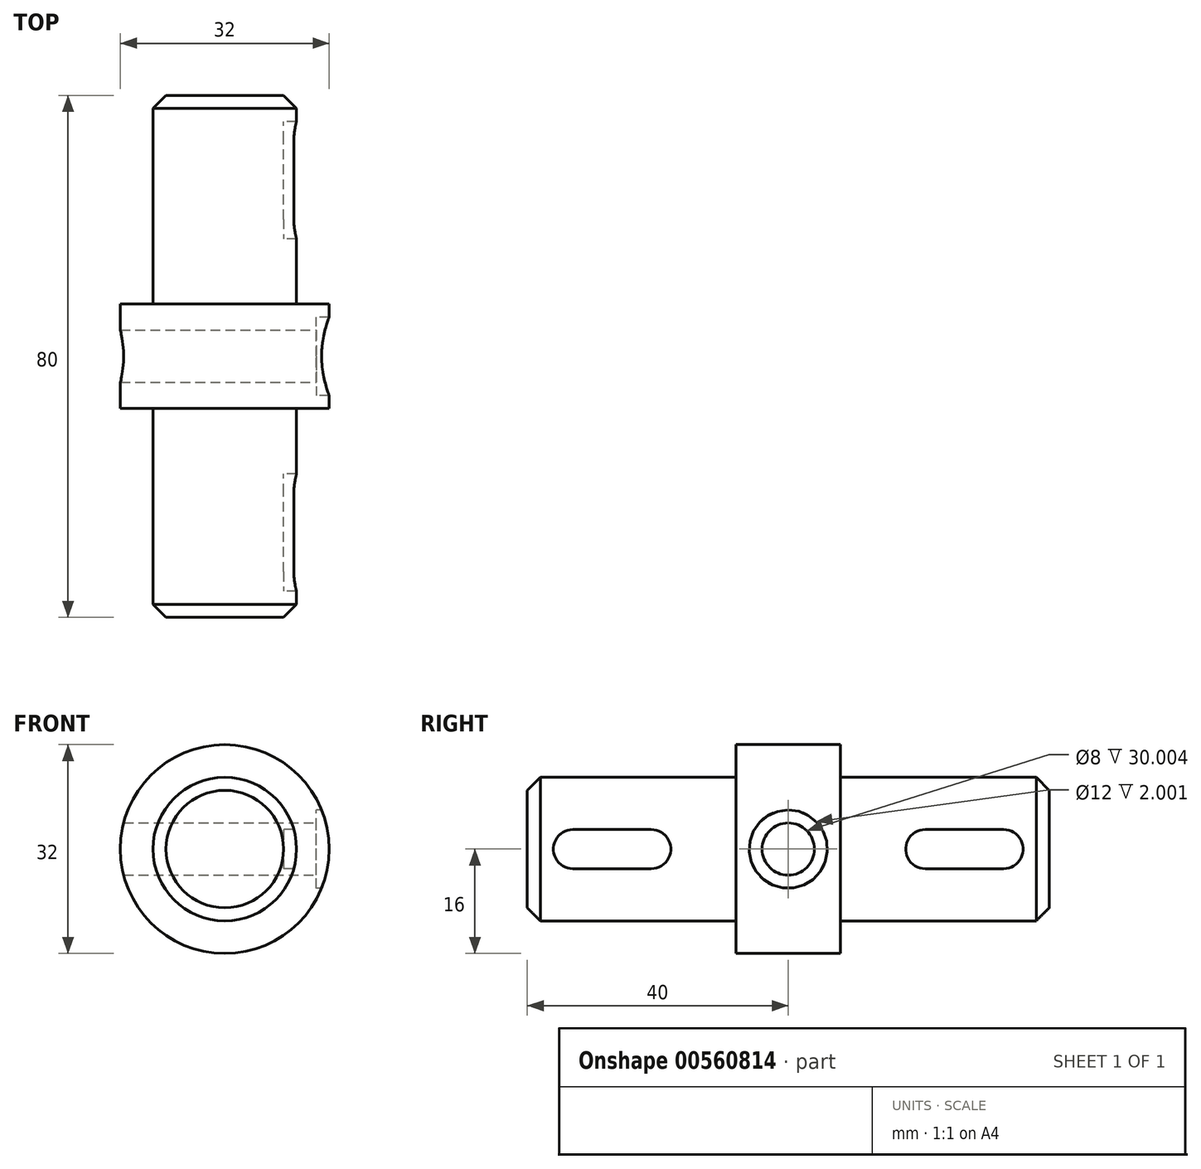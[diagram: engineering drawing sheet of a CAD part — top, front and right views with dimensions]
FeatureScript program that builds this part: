
annotation { "Feature Type Name" : "Feature", "Feature Type Description" : "" }
export const myFeature = defineFeature(function(context is Context, id is Id, definition is map)
    precondition{}
    {
        {
            var Q0;
            Q0=qCreatedBy(makeId("Front.planeOp"),FACE);
            var sketch = newSketch(context, id + "F0", { "sketchPlane" : qUnion([Q0])});
            skCircle(sketch, "E0", {"center": v(0, 0) * mm, "radius": 11 * mm});
            skSolve(sketch);
        }
        {
            var Q0;
            Q0 = qSketchRegion(id + "F0", true);
            extrude(context, id + "F1", {"entities" : qUnion([Q0]), "endBound" : BoundingType.SYMMETRIC, "depth" : 80 * mm, "offsetDistance" : 25 * mm});
        }
        {
            var Q0;
            Q0=qCreatedBy(makeId("Front.planeOp"),FACE);
            var sketch = newSketch(context, id + "F2", { "sketchPlane" : qUnion([Q0])});
            skCircle(sketch, "E1", {"center": v(0, 0) * mm, "radius": 16 * mm});
            skSolve(sketch);
        }
        {
            var Q0;
            Q0 = qSketchRegion(id + "F2", true);
            extrude(context, id + "F3", {"entities" : qUnion([Q0]), "operationType" : NewBodyOperationType.ADD, "endBound" : BoundingType.SYMMETRIC, "depth" : 16 * mm, "offsetDistance" : 25 * mm});
        }
        {
            var Q0;
            Q0=qCreatedBy(makeId("Right.planeOp"),FACE);
            var sketch = newSketch(context, id + "F4", { "sketchPlane" : qUnion([Q0])});
            skCircle(sketch, "E2", {"center": v(0, 0) * mm, "radius": 4 * mm});
            skSolve(sketch);
        }
        {
            var Q0;
            Q0 = qSketchRegion(id + "F4", true);
            extrude(context, id + "F5", {"entities" : qUnion([Q0]), "operationType" : NewBodyOperationType.REMOVE, "endBound" : BoundingType.SYMMETRIC, "oppositeDirection" : true, "depth" : 50 * mm, "offsetDistance" : 25 * mm});
        }
        {
            var Q0;
            Q0=qCreatedBy(makeId("Right.planeOp"),FACE);
            var sketch = newSketch(context, id + "F6", { "sketchPlane" : qUnion([Q0])});
            skCircle(sketch, "E3", {"center": v(0, 0) * mm, "radius": 6 * mm});
            skSolve(sketch);
        }
        {
            var Q0;
            Q0 = qSketchRegion(id + "F6", true);
            extrude(context, id + "F7", {"entities" : qUnion([Q0]), "operationType" : NewBodyOperationType.REMOVE, "depth" : 25 * mm, "offsetDistance" : 25 * mm});
        }
        {
            var Q0;
            Q0=qCreatedBy(makeId("Right.planeOp"),FACE);
            var sketch = newSketch(context, id + "F8", { "sketchPlane" : qUnion([Q0])});
            skCircle(sketch, "E4", {"center": v(0, 0) * mm, "radius": 6 * mm});
            skCircle(sketch, "E5", {"center": v(0, 0) * mm, "radius": 4 * mm});
            skSolve(sketch);
        }
        {
            var Q0;
            Q0 = qSketchRegion(id + "F8", true);
            extrude(context, id + "F9", {"entities" : qUnion([Q0]), "operationType" : NewBodyOperationType.ADD, "depth" : 14 * mm, "offsetDistance" : 25 * mm});
        }
        {
            var Q0;
            Q0=qCreatedBy(makeId("Right.planeOp"),FACE);
            var sketch = newSketch(context, id + "F10", { "sketchPlane" : qUnion([Q0])});
            skLineSegment(sketch, "E6", {"start": v(0, 0) * mm, "end": v(-8, 0) * mm});
            skLineSegment(sketch, "E7", {"start": v(-8, 0) * mm, "end": v(-21, 0) * mm});
            skLineSegment(sketch, "E8", {"start": v(-33, 3) * mm, "end": v(-21, 3) * mm});
            skLineSegment(sketch, "E9", {"start": v(-21, -3) * mm, "end": v(-33, -3) * mm});
            skArc(sketch, "E10", {"start": v(-21, -3) * mm, "mid": v(-18, 0) * mm, "end": v(-21, 3) * mm});
            skArc(sketch, "E11", {"start": v(-33, 3) * mm, "mid": v(-36, 0) * mm, "end": v(-33, -3) * mm});
            skLineSegment(sketch, "E12", {"start": v(-21, 0) * mm, "end": v(-33, 0) * mm});
            skLineSegment(sketch, "E13", {"start": v(0, 0) * mm, "end": v(21, 0) * mm});
            skLineSegment(sketch, "E14", {"start": v(21, 0) * mm, "end": v(33, 0) * mm});
            skLineSegment(sketch, "E15", {"start": v(33, -3) * mm, "end": v(21, -3) * mm});
            skLineSegment(sketch, "E16", {"start": v(21, 3) * mm, "end": v(33, 3) * mm});
            skLineSegment(sketch, "E17", {"start": v(33, 3) * mm, "end": v(33, 0) * mm});
            skArc(sketch, "E18", {"start": v(21, 3) * mm, "mid": v(18, 0) * mm, "end": v(21, -3) * mm});
            skArc(sketch, "E19", {"start": v(33, -3) * mm, "mid": v(36, 0) * mm, "end": v(33, 3) * mm});
            skSolve(sketch);
        }
        {
            var Q0;
            Q0 = qSketchRegion(id + "F10", true);
            extrude(context, id + "F11", {"entities" : qUnion([Q0]), "operationType" : NewBodyOperationType.REMOVE, "depth" : 25 * mm, "offsetDistance" : 25 * mm});
        }
        {
            var Q0;
            Q0=qCreatedBy(makeId("Right.planeOp"),FACE);
            var sketch = newSketch(context, id + "F12", { "sketchPlane" : qUnion([Q0])});
            skLineSegment(sketch, "E20", {"start": v(0, 0) * mm, "end": v(-18, 0) * mm});
            skLineSegment(sketch, "E21", {"start": v(0, 0) * mm, "end": v(18, 0) * mm});
            skPoint(sketch, "E22.endSnap0", {"position": v(10.5, 0) * mm});
            skLineSegment(sketch, "E23.bottom", {"start": v(-33, 3) * mm, "end": v(-21, 3) * mm});
            skLineSegment(sketch, "E23.top", {"start": v(-33, -3) * mm, "end": v(-21, -3) * mm});
            skLineSegment(sketch, "E24.bottom", {"start": v(21, 3) * mm, "end": v(33.11, 3) * mm});
            skLineSegment(sketch, "E24.top", {"start": v(21, -3) * mm, "end": v(33.11, -3) * mm});
            skArc(sketch, "E25", {"start": v(-33, 3) * mm, "mid": v(-36, 0) * mm, "end": v(-33, -3) * mm});
            skArc(sketch, "E26", {"start": v(-21, -3) * mm, "mid": v(-18, 0) * mm, "end": v(-21, 3) * mm});
            skArc(sketch, "E27", {"start": v(21, 3) * mm, "mid": v(18, 0) * mm, "end": v(21, -3) * mm});
            skArc(sketch, "E28", {"start": v(33.11, -3) * mm, "mid": v(36.11, 0) * mm, "end": v(33.11, 3) * mm});
            skPoint(sketch, "E22.end.orphan", {"position": v(33, 0) * mm});
            skSolve(sketch);
        }
        {
            var Q0;
            Q0 = qSketchRegion(id + "F12", true);
            extrude(context, id + "F13", {"entities" : qUnion([Q0]), "operationType" : NewBodyOperationType.ADD, "depth" : 9 * mm, "offsetDistance" : 25 * mm});
        }
        {
            var Q0;
            Q0=makeQuery(id+"F1.opExtrude","CAP_EDGE",EDGE,{"disambiguationData":[OSD([sQuery(id+"F0.wireOp",EDGE,"E0")])],"isStart":true});
            var Q1;
            Q1=makeQuery(id+"F1.opExtrude","CAP_EDGE",EDGE,{"disambiguationData":[OSD([sQuery(id+"F0.wireOp",EDGE,"E0")])],"isStart":false});
            chamfer(context, id + "F14", {"entities" : qUnion([Q0, Q1]), "chamferType" : ChamferType.OFFSET_ANGLE, "width" : 2 * mm, "oppositeDirection" : false, "angle" : 45 * degree, "tangentPropagation" : true});
        }
    });
